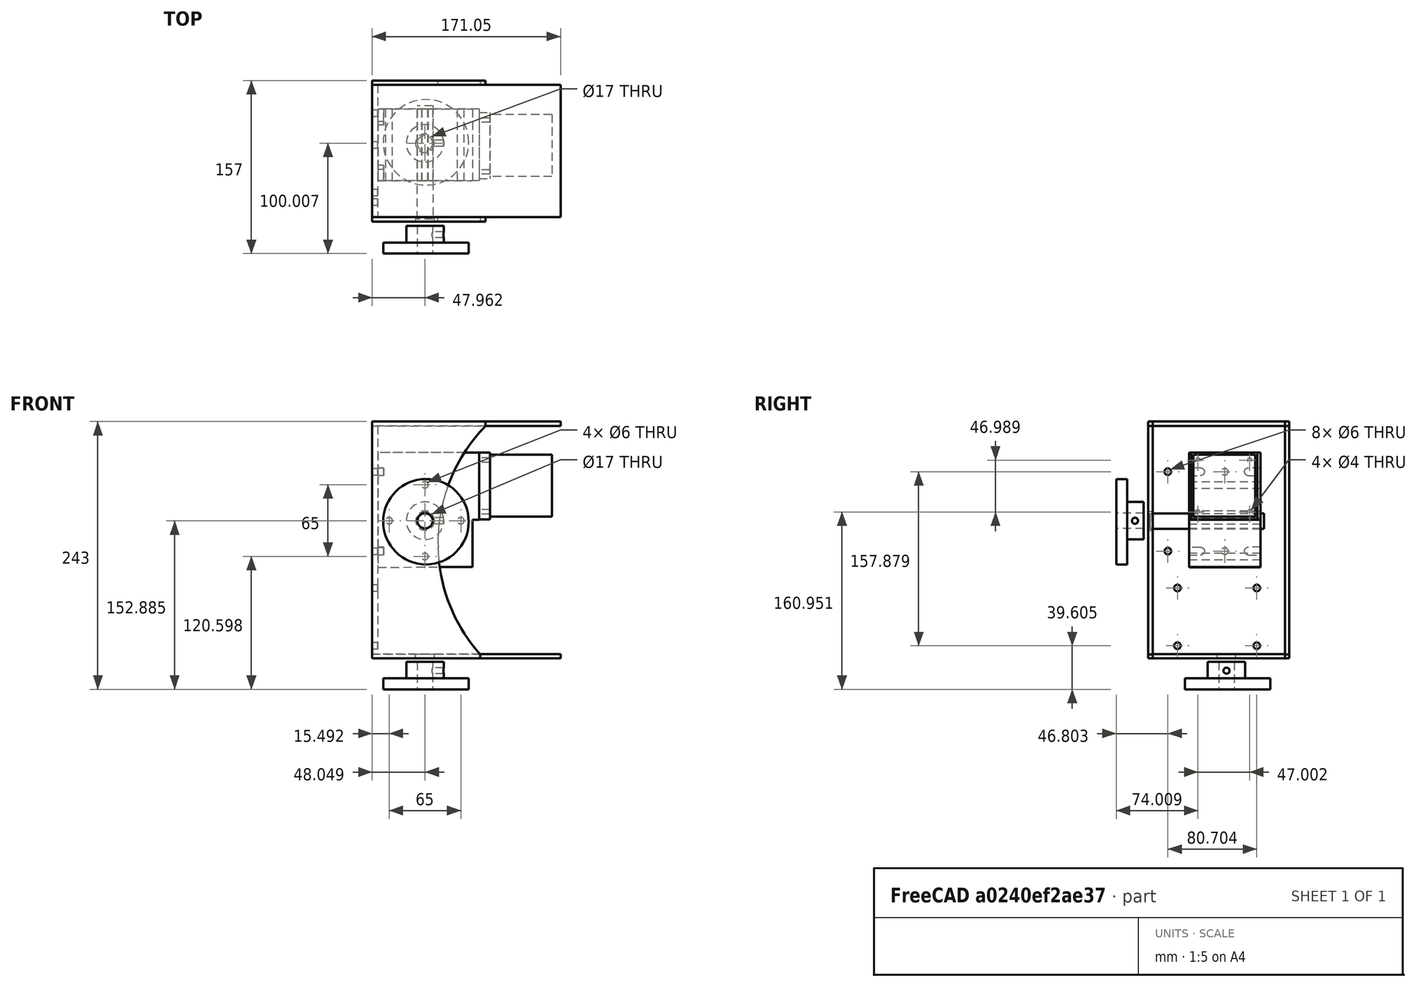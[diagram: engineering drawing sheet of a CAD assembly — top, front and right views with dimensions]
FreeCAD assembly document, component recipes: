
FREECAD ASSEMBLY — COMPONENT RECIPES ("az-el-rotor")

This assembly document has 15 components, labeled P0..P14 below (a component is one placed body or linked part). 15 of them carry a construction recipe — the FreeCAD feature program that regenerates the part from scratch, quoted from this document or its linked companion documents; the rest are supplied as boundary geometry only. No exploded tour is included for this assembly.
COMPONENT P0 — recipe-attached ("back-plate", modeled in this document).
Construction recipe (the document's own serialized feature program — sketch geometry with constraints, then the solid features built on it; lengths are millimeters unless a unit is written):

FEATURE [Sketcher::SketchObject] Sketch009
  MapMode = 5
  Placement = pos=(0,0,0) rot=(0.57735,0.57735,0.57735;2.0944rad)
  Support = -> [YZ_Plane004]
  sketch-geometry (24):
    g0: LineSegment [constr] StartX=-28 StartY=-262 StartZ=0 EndX=78 EndY=-262 EndZ=0
    g1: LineSegment [constr] StartX=78 StartY=-262 StartZ=0 EndX=78 EndY=-263 EndZ=0
    g2: LineSegment [constr] StartX=78 StartY=-263 StartZ=0 EndX=-28 EndY=-263 EndZ=0
    g3: LineSegment [constr] StartX=-28 StartY=-263 StartZ=0 EndX=-28 EndY=-262 EndZ=0
    g4: LineSegment [constr] StartX=78 StartY=-263 StartZ=0 EndX=88 EndY=-263 EndZ=0
    g5: LineSegment [constr] StartX=88 StartY=-263 StartZ=0 EndX=88 EndY=-80 EndZ=0
    g6: LineSegment [constr] StartX=88 StartY=-80 StartZ=0 EndX=78 EndY=-80 EndZ=0
    g7: LineSegment [constr] StartX=78 StartY=-80 StartZ=0 EndX=78 EndY=-263 EndZ=0
    g8: LineSegment [constr] StartX=88 StartY=-80 StartZ=0 EndX=78 EndY=-80 EndZ=0
    g9: LineSegment [constr] StartX=78 StartY=-80 StartZ=0 EndX=78 EndY=-60 EndZ=0
    g10: LineSegment [constr] StartX=78 StartY=-60 StartZ=0 EndX=88 EndY=-60 EndZ=0
    g11: LineSegment [constr] StartX=88 StartY=-60 StartZ=0 EndX=88 EndY=-80 EndZ=0
    g12: LineSegment [constr] StartX=88 StartY=-60 StartZ=0 EndX=-41 EndY=-60 EndZ=0
    g13: LineSegment [constr] StartX=-41 StartY=-60 StartZ=0 EndX=-41 EndY=-56 EndZ=0
    g14: LineSegment [constr] StartX=-41 StartY=-56 StartZ=0 EndX=88 EndY=-56 EndZ=0
    g15: LineSegment [constr] StartX=88 StartY=-56 StartZ=0 EndX=88 EndY=-60 EndZ=0
    g16: LineSegment [constr] StartX=-28 StartY=-263 StartZ=0 EndX=-32 EndY=-263 EndZ=0
    g17: LineSegment [constr] StartX=-32 StartY=-263 StartZ=0 EndX=-32 EndY=-53 EndZ=0
    g18: LineSegment [constr] StartX=-32 StartY=-53 StartZ=0 EndX=-28 EndY=-53 EndZ=0
    g19: LineSegment [constr] StartX=-28 StartY=-53 StartZ=0 EndX=-28 EndY=-263 EndZ=0
    g20: LineSegment StartX=88 StartY=-263 StartZ=0 EndX=-32 EndY=-263 EndZ=0
    g21: LineSegment StartX=-32 StartY=-263 StartZ=0 EndX=-32 EndY=-56 EndZ=0
    g22: LineSegment StartX=-32 StartY=-56 StartZ=0 EndX=88 EndY=-56 EndZ=0
    g23: LineSegment StartX=88 StartY=-56 StartZ=0 EndX=88 EndY=-263 EndZ=0
  constraints (53):
    c: Coincident(g0,g1)
    c: Coincident(g1,g2)
    c: Coincident(g2,g3)
    c: Coincident(g3,g0)
    c: Horizontal(g0)
    c: Horizontal(g2)
    c: Vertical(g1)
    c: Vertical(g3)
    c: Coincident(g4,g5)
    c: Coincident(g5,g6)
    c: Coincident(g6,g7)
    c: Coincident(g7,g4)
    c: Horizontal(g4)
    c: Horizontal(g6)
    c: Vertical(g5)
    c: Vertical(g7)
    c: Coincident(g4,g1)
    c: Coincident(g8,g9)
    c: Coincident(g9,g10)
    c: Coincident(g10,g11)
    c: Coincident(g11,g8)
    c: Horizontal(g8)
    c: Horizontal(g10)
    c: Vertical(g9)
    c: Vertical(g11)
    c: Coincident(g12,g13)
    c: Coincident(g13,g14)
    c: Coincident(g14,g15)
    c: Coincident(g15,g12)
    c: Horizontal(g12)
    c: Horizontal(g14)
    c: Vertical(g13)
    c: Vertical(g15)
    c: Coincident(g12,g10)
    c: Coincident(g16,g17)
    c: Coincident(g17,g18)
    c: Coincident(g18,g19)
    c: Coincident(g19,g16)
    c: Horizontal(g16)
    c: Horizontal(g18)
    c: Vertical(g17)
    c: Vertical(g19)
    c: Coincident(g16,g2)
    c: Coincident(g20,g21)
    c: Coincident(g21,g22)
    c: Coincident(g22,g23)
    c: Coincident(g23,g20)
    c: Horizontal(g20)
    c: Horizontal(g22)
    c: Vertical(g21)
    c: Vertical(g23)
    c: Coincident(g20,g4)
    c: PointOnObject(g21,g17)
FEATURE [PartDesign::Pad] Pad004
  AllowMultiFace = false
  Direction = (1,1,1)
  Length = 5
  Length2 = 100
  Placement = pos=(0,0,0) rot=(0.57735,0.57735,0.57735;2.0944rad)
  Profile = -> Sketch009
  Type = 0
FEATURE [Sketcher::SketchObject] Sketch010
  MapMode = 5
  Placement = pos=(4e-16,0,0) rot=(0.57735,0.57735,-0.57735;4.18879rad)
  Support = -> [Pad004]
  sketch-geometry (16):
    g0: Circle CenterX=33.537 CenterY=97.5713 CenterZ=0 NormalX=0 NormalY=0 NormalZ=1 AngleXU=0 Radius=3.67394
    g1: Circle CenterX=-18.1974 CenterY=97.5163 CenterZ=0 NormalX=0 NormalY=0 NormalZ=1 AngleXU=0 Radius=3.49495
    g2: LineSegment [constr] StartX=33.537 StartY=97.5713 StartZ=0 EndX=-18.1875 EndY=97.5713 EndZ=0
    g3: LineSegment [constr] StartX=-18.1875 StartY=97.5713 StartZ=0 EndX=-18.1875 EndY=169.553 EndZ=0
    g4: LineSegment [constr] StartX=-18.1875 StartY=169.553 StartZ=0 EndX=33.537 EndY=169.553 EndZ=0
    g5: LineSegment [constr] StartX=33.537 StartY=169.553 StartZ=0 EndX=33.537 EndY=97.5713 EndZ=0
    g6: Circle CenterX=-18.1875 CenterY=169.553 CenterZ=0 NormalX=0 NormalY=0 NormalZ=1 AngleXU=0 Radius=3.5641
    g7: Circle CenterX=33.537 CenterY=169.553 CenterZ=0 NormalX=0 NormalY=0 NormalZ=1 AngleXU=0 Radius=3.59605
    g8: LineSegment [constr] StartX=-9.48692 StartY=255.395 StartZ=0 EndX=62.5067 EndY=255.395 EndZ=0
    g9: LineSegment [constr] StartX=62.5067 StartY=255.395 StartZ=0 EndX=62.5067 EndY=203.001 EndZ=0
    g10: LineSegment [constr] StartX=62.5067 StartY=203.001 StartZ=0 EndX=-9.48692 EndY=203.001 EndZ=0
    g11: LineSegment [constr] StartX=-9.48692 StartY=203.001 StartZ=0 EndX=-9.48692 EndY=255.395 EndZ=0
    g12: Circle CenterX=-9.48692 CenterY=255.395 CenterZ=0 NormalX=0 NormalY=0 NormalZ=1 AngleXU=0 Radius=3.50608
    g13: Circle CenterX=62.5067 CenterY=255.395 CenterZ=0 NormalX=0 NormalY=0 NormalZ=1 AngleXU=0 Radius=3.47701
    g14: Circle CenterX=62.5067 CenterY=203.001 CenterZ=0 NormalX=0 NormalY=0 NormalZ=1 AngleXU=0 Radius=3.61631
    g15: Circle CenterX=-9.48692 CenterY=203.001 CenterZ=0 NormalX=0 NormalY=0 NormalZ=1 AngleXU=0 Radius=3.60277
  constraints (23):
    c: Coincident(g2,g3)
    c: Coincident(g3,g4)
    c: Coincident(g4,g5)
    c: Coincident(g5,g2)
    c: Horizontal(g2)
    c: Horizontal(g4)
    c: Vertical(g3)
    c: Vertical(g5)
    c: Coincident(g2,g0)
    c: Coincident(g6,g3)
    c: Coincident(g7,g4)
    c: Coincident(g8,g9)
    c: Coincident(g9,g10)
    c: Coincident(g10,g11)
    c: Coincident(g11,g8)
    c: Horizontal(g8)
    c: Horizontal(g10)
    c: Vertical(g9)
    c: Vertical(g11)
    c: Coincident(g12,g8)
    c: Coincident(g13,g8)
    c: Coincident(g14,g9)
    c: Coincident(g15,g10)
FEATURE [PartDesign::Hole] Hole002
  AllowMultiFace = false
  BaseFeature = -> Pad004
  Depth = 7
  DepthType = 0
  Diameter = 6
  DrillPoint = 1
  DrillPointAngle = 118
  HoleCutCountersinkAngle = 90
  HoleCutDepth = 0
  HoleCutDiameter = 0
  HoleCutType = 0
  ModelActualThread = false
  Placement = pos=(0,0,0) rot=(0.57735,0.57735,0.57735;2.0944rad)
  Profile = -> Sketch010
  Tapered = false
  TaperedAngle = 90
  ThreadAngle = 0
  ThreadClass = 0
  ThreadCutOffInner = 0
  ThreadCutOffOuter = 0
  ThreadDirection = 0
  ThreadFit = 0
  ThreadPitch = 0
  ThreadSize = 0
  ThreadType = 0
  Threaded = false
FEATURE [PartDesign::Body] Body004  label="back-plate"
  Group = -> [Sketch009,Pad004,Sketch010,Hole002]
  Origin = -> Origin004
  Placement = pos=(-94,0,0) rot=(0,0,1;0rad)
  Tip = -> Hole002
COMPONENT P1 — recipe-attached ("top-plate", modeled in this document).
Construction recipe (the document's own serialized feature program — sketch geometry with constraints, then the solid features built on it; lengths are millimeters unless a unit is written):

FEATURE [Sketcher::SketchObject] Sketch011
  MapMode = 5
  Support = -> [XY_Plane005]
  sketch-geometry (4):
    g0: LineSegment StartX=-94 StartY=88 StartZ=0 EndX=77.053 EndY=88 EndZ=0
    g1: LineSegment StartX=77.053 StartY=88 StartZ=0 EndX=77.053 EndY=-32 EndZ=0
    g2: LineSegment StartX=77.053 StartY=-32 StartZ=0 EndX=-94 EndY=-32 EndZ=0
    g3: LineSegment StartX=-94 StartY=-32 StartZ=0 EndX=-94 EndY=88 EndZ=0
  constraints (8):
    c: Coincident(g0,g1)
    c: Coincident(g1,g2)
    c: Coincident(g2,g3)
    c: Coincident(g3,g0)
    c: Horizontal(g0)
    c: Horizontal(g2)
    c: Vertical(g1)
    c: Vertical(g3)
FEATURE [PartDesign::Pad] Pad005
  AllowMultiFace = false
  Direction = (1,1,1)
  Length = 4
  Length2 = 100
  Profile = -> Sketch011
  Type = 0
FEATURE [PartDesign::Body] Body005  label="top-plate"
  Group = -> [Sketch011,Pad005]
  Origin = -> Origin005
  Placement = pos=(0,0,-56) rot=(0,0,1;0rad)
  Tip = -> Pad005
COMPONENT P2 — recipe-attached ("bottom-plate", modeled in this document).
Construction recipe (the document's own serialized feature program — sketch geometry with constraints, then the solid features built on it; lengths are millimeters unless a unit is written):

FEATURE [Sketcher::SketchObject] Sketch012
  MapMode = 5
  Support = -> [XY_Plane006]
  sketch-geometry (4):
    g0: LineSegment StartX=-93.9912 StartY=88.0053 StartZ=0 EndX=77 EndY=88.0053 EndZ=0
    g1: LineSegment StartX=77 StartY=88.0053 StartZ=0 EndX=77 EndY=-32 EndZ=0
    g2: LineSegment StartX=77 StartY=-32 StartZ=0 EndX=-93.9912 EndY=-32 EndZ=0
    g3: LineSegment StartX=-93.9912 StartY=-32 StartZ=0 EndX=-93.9912 EndY=88.0053 EndZ=0
  constraints (8):
    c: Coincident(g0,g1)
    c: Coincident(g1,g2)
    c: Coincident(g2,g3)
    c: Coincident(g3,g0)
    c: Horizontal(g0)
    c: Horizontal(g2)
    c: Vertical(g1)
    c: Vertical(g3)
FEATURE [PartDesign::Pad] Pad006
  AllowMultiFace = false
  Direction = (1,1,1)
  Length = 4
  Length2 = 100
  Profile = -> Sketch012
  Type = 0
FEATURE [Sketcher::SketchObject] Sketch013
  MapMode = 5
  Placement = pos=(0,0,0) rot=(1,0,0;3.14159rad)
  Support = -> [Pad006]
  sketch-geometry (1):
    g0: Circle CenterX=-46.0384 CenterY=-35.0069 CenterZ=0 NormalX=0 NormalY=0 NormalZ=1 AngleXU=0 Radius=10.0299
FEATURE [PartDesign::Hole] Hole003
  AllowMultiFace = false
  BaseFeature = -> Pad006
  Depth = 10
  DepthType = 0
  Diameter = 17
  DrillPoint = 1
  DrillPointAngle = 118
  HoleCutCountersinkAngle = 90
  HoleCutDepth = 0
  HoleCutDiameter = 0
  HoleCutType = 0
  ModelActualThread = false
  Profile = -> Sketch013
  Tapered = false
  TaperedAngle = 90
  ThreadAngle = 0
  ThreadClass = 0
  ThreadCutOffInner = 0
  ThreadCutOffOuter = 0
  ThreadDirection = 0
  ThreadFit = 0
  ThreadPitch = 0
  ThreadSize = 0
  ThreadType = 0
  Threaded = false
FEATURE [PartDesign::Body] Body006  label="bottom-plate"
  Group = -> [Sketch012,Pad006,Sketch013,Hole003]
  Origin = -> Origin006
  Placement = pos=(0,0,-267) rot=(0,0,1;0rad)
  Tip = -> Hole003
COMPONENT P3 — recipe-attached ("adapter", modeled in this document).
Construction recipe (the document's own serialized feature program — sketch geometry with constraints, then the solid features built on it; lengths are millimeters unless a unit is written):

FEATURE [Sketcher::SketchObject] Sketch014
  MapMode = 5
  Support = -> [XY_Plane007]
  sketch-geometry (1):
    g0: Circle CenterX=-46.1126 CenterY=35.0755 CenterZ=0 NormalX=0 NormalY=0 NormalZ=1 AngleXU=0 Radius=38.7738
FEATURE [PartDesign::Pad] Pad007
  AllowMultiFace = false
  Direction = (1,1,1)
  Length = 10
  Length2 = 100
  Profile = -> Sketch014
  Type = 0
FEATURE [Sketcher::SketchObject] Sketch015
  MapMode = 5
  Placement = pos=(0,0,0) rot=(1,0,0;3.14159rad)
  Support = -> [Pad007]
  sketch-geometry (4):
    g0: LineSegment [constr] StartX=-47 StartY=5 StartZ=0 EndX=-47 EndY=-81 EndZ=0
    g1: LineSegment [constr] StartX=-86 StartY=-36 StartZ=0 EndX=-6 EndY=-36 EndZ=0
    g2: Circle [constr] CenterX=-47 CenterY=-36 CenterZ=0 NormalX=0 NormalY=0 NormalZ=1 AngleXU=0 Radius=7
    g3: Circle CenterX=-47 CenterY=-36 CenterZ=0 NormalX=0 NormalY=0 NormalZ=1 AngleXU=0 Radius=17
  constraints (5):
    c: Vertical(g0)
    c: Horizontal(g1)
    c: PointOnObject(g2,g0)
    c: Diameter(g2) = 14
    c: Coincident(g3,g2)
FEATURE [PartDesign::Pad] Pad008
  AllowMultiFace = false
  BaseFeature = -> Pad007
  Direction = (1,1,1)
  Length = 15
  Length2 = 100
  Profile = -> Sketch015
  Type = 0
FEATURE [Sketcher::SketchObject] Sketch016
  MapMode = 5
  Placement = pos=(0,0,-15) rot=(1,0,0;3.14159rad)
  Support = -> [Pad008]
  sketch-geometry (3):
    g0: LineSegment [constr] StartX=-47.0041 StartY=-17.9869 StartZ=0 EndX=-47.0041 EndY=-57.2105 EndZ=0
    g1: LineSegment [constr] StartX=-67.0883 StartY=-35.9976 StartZ=0 EndX=-26.7183 EndY=-35.9976 EndZ=0
    g2: Circle CenterX=-47.0247 CenterY=-35.9976 CenterZ=0 NormalX=0 NormalY=0 NormalZ=1 AngleXU=0 Radius=7
  constraints (4):
    c: Vertical(g0)
    c: Horizontal(g1)
    c: PointOnObject(g2,g1)
    c: Diameter(g2) = 14
FEATURE [PartDesign::Hole] Hole004
  AllowMultiFace = false
  BaseFeature = -> Pad008
  Depth = 33
  DepthType = 0
  Diameter = 14
  DrillPoint = 1
  DrillPointAngle = 118
  HoleCutCountersinkAngle = 90
  HoleCutDepth = 0
  HoleCutDiameter = 0
  HoleCutType = 0
  ModelActualThread = false
  Profile = -> Sketch016
  Tapered = false
  TaperedAngle = 90
  ThreadAngle = 0
  ThreadClass = 0
  ThreadCutOffInner = 0
  ThreadCutOffOuter = 0
  ThreadDirection = 0
  ThreadFit = 0
  ThreadPitch = 0
  ThreadSize = 0
  ThreadType = 0
  Threaded = false
FEATURE [Sketcher::SketchObject] Sketch017
  MapMode = 5
  Placement = pos=(0,0,0) rot=(0.57735,0.57735,0.57735;2.0944rad)
  Support = -> [YZ_Plane007]
  sketch-geometry (1):
    g0: Circle CenterX=35.9745 CenterY=-6.96869 CenterZ=0 NormalX=0 NormalY=0 NormalZ=1 AngleXU=0 Radius=2.5
  constraints (1):
    c: Diameter(g0) = 5
FEATURE [PartDesign::Hole] Hole005
  AllowMultiFace = false
  BaseFeature = -> Hole004
  Depth = 43
  DepthType = 0
  Diameter = 5.5
  DrillPoint = 1
  DrillPointAngle = 118
  HoleCutCountersinkAngle = 90
  HoleCutDepth = 0
  HoleCutDiameter = 5
  HoleCutType = 0
  ModelActualThread = false
  Profile = -> Sketch017
  Tapered = false
  TaperedAngle = 90
  ThreadAngle = 60
  ThreadClass = 0
  ThreadCutOffInner = 0.0866025
  ThreadCutOffOuter = 0.173205
  ThreadDirection = 0
  ThreadFit = 0
  ThreadPitch = 0.8
  ThreadSize = 0
  ThreadType = 0
  Threaded = false
FEATURE [PartDesign::Body] Body007  label="adapter"
  Group = -> [Sketch014,Pad007,Sketch015,Pad008,Sketch016,Hole004,Sketch017,Hole005]
  Origin = -> Origin007
  Placement = pos=(1,71,-285) rot=(1,0,0;3.14159rad)
  Tip = -> Hole005
COMPONENT P4 — recipe-attached ("sideplate1", modeled in this document).
Construction recipe (the document's own serialized feature program — sketch geometry with constraints, then the solid features built on it; lengths are millimeters unless a unit is written):

FEATURE [Sketcher::SketchObject] Sketch018
  MapMode = 5
  Placement = pos=(0,0,0) rot=(1,0,0;1.5708rad)
  Support = -> [XZ_Plane008]
  sketch-geometry (7):
    g0: LineSegment StartX=-94 StartY=-52 StartZ=0 EndX=-94 EndY=-267 EndZ=0
    g1: LineSegment StartX=-94 StartY=-267 StartZ=0 EndX=3.97419 EndY=-267 EndZ=0
    g2: LineSegment StartX=9 StartY=-52 StartZ=0 EndX=-94 EndY=-52 EndZ=0
    g3: Circle [constr] CenterX=9 CenterY=-52 CenterZ=0 NormalX=0 NormalY=0 NormalZ=1 AngleXU=0 Radius=10
    g4: LineSegment StartX=9 StartY=-52 StartZ=0 EndX=9 EndY=-56 EndZ=0
    g5: LineSegment StartX=3.97419 StartY=-267 StartZ=0 EndX=3.97419 EndY=-263.283 EndZ=0
    g6: ArcOfCircle CenterX=117.845 CenterY=-162.341 CenterZ=0 NormalX=0 NormalY=0 NormalZ=1 AngleXU=0 Radius=152.17 StartAngle=2.36783 EndAngle=3.86687
  constraints (12):
    c: Vertical(g0)
    c: Coincident(g0,g1)
    c: Horizontal(g1)
    c: Coincident(g2,g0)
    c: Horizontal(g2)
    c: Coincident(g3,g2)
    c: Coincident(g4,g2)
    c: Vertical(g4)
    c: Vertical(g5)
    c: Coincident(g6,g4)
    c: Coincident(g6,g5)
    c: Coincident(g1,g5)
FEATURE [PartDesign::Pad] Pad009
  AllowMultiFace = false
  Direction = (1,1,1)
  Length = 4
  Length2 = 100
  Placement = pos=(0,0,0) rot=(1,0,0;1.5708rad)
  Profile = -> Sketch018
  Type = 0
FEATURE [Sketcher::SketchObject] Sketch020
  MapMode = 5
  Placement = pos=(0,-4,9e-16) rot=(1,0,0;1.5708rad)
  Support = -> [Pad009]
  sketch-geometry (1):
    g0: Circle CenterX=-45.9514 CenterY=-142.115 CenterZ=0 NormalX=0 NormalY=0 NormalZ=1 AngleXU=0 Radius=8.75
  constraints (1):
    c: Diameter(g0) = 17.5
FEATURE [PartDesign::Hole] Hole006
  AllowMultiFace = false
  BaseFeature = -> Pad009
  Depth = 25
  DepthType = 0
  Diameter = 17
  DrillPoint = 1
  DrillPointAngle = 118
  HoleCutCountersinkAngle = 90
  HoleCutDepth = 0
  HoleCutDiameter = 0
  HoleCutType = 0
  ModelActualThread = false
  Placement = pos=(0,0,0) rot=(1,0,0;1.5708rad)
  Profile = -> Sketch020
  Tapered = false
  TaperedAngle = 90
  ThreadAngle = 0
  ThreadClass = 0
  ThreadCutOffInner = 0
  ThreadCutOffOuter = 0
  ThreadDirection = 0
  ThreadFit = 0
  ThreadPitch = 0
  ThreadSize = 0
  ThreadType = 0
  Threaded = false
FEATURE [PartDesign::Body] Body008  label="sideplate1"
  Group = -> [Sketch018,Pad009,Sketch020,Hole006]
  Origin = -> Origin008
  Placement = pos=(0,-32,0) rot=(0,0,1;0rad)
  Tip = -> Hole006
COMPONENT P5 — recipe-attached ("sideplate002", modeled in this document).
Construction recipe (the document's own serialized feature program — sketch geometry with constraints, then the solid features built on it; lengths are millimeters unless a unit is written):

FEATURE [Sketcher::SketchObject] Sketch019
  MapMode = 5
  Placement = pos=(0,0,0) rot=(1,0,0;1.5708rad)
  Support = -> [XZ_Plane009]
  sketch-geometry (7):
    g0: LineSegment StartX=-94 StartY=-52 StartZ=0 EndX=-94 EndY=-267 EndZ=0
    g1: LineSegment StartX=-94 StartY=-267 StartZ=0 EndX=3.97419 EndY=-267 EndZ=0
    g2: LineSegment StartX=9 StartY=-52 StartZ=0 EndX=-94 EndY=-52 EndZ=0
    g3: Circle [constr] CenterX=9 CenterY=-52 CenterZ=0 NormalX=0 NormalY=0 NormalZ=1 AngleXU=0 Radius=10
    g4: LineSegment StartX=9 StartY=-52 StartZ=0 EndX=9 EndY=-56 EndZ=0
    g5: LineSegment StartX=3.97419 StartY=-267 StartZ=0 EndX=3.97419 EndY=-263.283 EndZ=0
    g6: ArcOfCircle CenterX=117.845 CenterY=-162.341 CenterZ=0 NormalX=0 NormalY=0 NormalZ=1 AngleXU=0 Radius=152.17 StartAngle=2.36783 EndAngle=3.86687
  constraints (12):
    c: Vertical(g0)
    c: Coincident(g0,g1)
    c: Horizontal(g1)
    c: Coincident(g2,g0)
    c: Horizontal(g2)
    c: Coincident(g3,g2)
    c: Coincident(g4,g2)
    c: Vertical(g4)
    c: Vertical(g5)
    c: Coincident(g6,g4)
    c: Coincident(g6,g5)
    c: Coincident(g1,g5)
FEATURE [PartDesign::Pad] Pad010
  AllowMultiFace = false
  Direction = (1,1,1)
  Length = 4
  Length2 = 100
  Placement = pos=(0,0,0) rot=(1,0,0;1.5708rad)
  Profile = -> Sketch019
  Type = 0
FEATURE [PartDesign::Body] Body009  label="sideplate002"
  Group = -> [Sketch019,Pad010]
  Origin = -> Origin009
  Placement = pos=(0,92,0) rot=(0,0,1;0rad)
  Tip = -> Pad010
COMPONENT P6 — recipe-attached ("adapter001", modeled in this document).
Construction recipe (the document's own serialized feature program — sketch geometry with constraints, then the solid features built on it; lengths are millimeters unless a unit is written):

FEATURE [Sketcher::SketchObject] Sketch021
  MapMode = 5
  Support = -> [XY_Plane010]
  sketch-geometry (1):
    g0: Circle CenterX=-46.1126 CenterY=35.0755 CenterZ=0 NormalX=0 NormalY=0 NormalZ=1 AngleXU=0 Radius=38.7738
FEATURE [PartDesign::Pad] Pad011
  AllowMultiFace = false
  Direction = (1,1,1)
  Length = 10
  Length2 = 100
  Profile = -> Sketch021
  Type = 0
FEATURE [Sketcher::SketchObject] Sketch022
  MapMode = 5
  Placement = pos=(0,0,0) rot=(0.57735,0.57735,0.57735;2.0944rad)
  Support = -> [YZ_Plane010]
  sketch-geometry (1):
    g0: Circle CenterX=35.9745 CenterY=-6.96869 CenterZ=0 NormalX=0 NormalY=0 NormalZ=1 AngleXU=0 Radius=2.5
  constraints (1):
    c: Diameter(g0) = 5
FEATURE [Sketcher::SketchObject] Sketch024
  MapMode = 5
  Placement = pos=(0,0,0) rot=(1,0,0;3.14159rad)
  Support = -> [Pad011]
  sketch-geometry (4):
    g0: LineSegment [constr] StartX=-47 StartY=5 StartZ=0 EndX=-47 EndY=-81 EndZ=0
    g1: LineSegment [constr] StartX=-86 StartY=-36 StartZ=0 EndX=-6 EndY=-36 EndZ=0
    g2: Circle [constr] CenterX=-47 CenterY=-36 CenterZ=0 NormalX=0 NormalY=0 NormalZ=1 AngleXU=0 Radius=7
    g3: Circle CenterX=-47 CenterY=-36 CenterZ=0 NormalX=0 NormalY=0 NormalZ=1 AngleXU=0 Radius=17
  constraints (5):
    c: Vertical(g0)
    c: Horizontal(g1)
    c: PointOnObject(g2,g0)
    c: Diameter(g2) = 14
    c: Coincident(g3,g2)
FEATURE [PartDesign::Pad] Pad012
  AllowMultiFace = false
  BaseFeature = -> Pad011
  Direction = (1,1,1)
  Length = 15
  Length2 = 100
  Profile = -> Sketch024
  Type = 0
FEATURE [Sketcher::SketchObject] Sketch023
  MapMode = 5
  Placement = pos=(0,0,-15) rot=(1,0,0;3.14159rad)
  Support = -> [Pad012]
  sketch-geometry (3):
    g0: LineSegment [constr] StartX=-47.0041 StartY=-17.9869 StartZ=0 EndX=-47.0041 EndY=-57.2105 EndZ=0
    g1: LineSegment [constr] StartX=-67.0883 StartY=-35.9976 StartZ=0 EndX=-26.7183 EndY=-35.9976 EndZ=0
    g2: Circle CenterX=-47.0247 CenterY=-35.9976 CenterZ=0 NormalX=0 NormalY=0 NormalZ=1 AngleXU=0 Radius=7
  constraints (4):
    c: Vertical(g0)
    c: Horizontal(g1)
    c: PointOnObject(g2,g1)
    c: Diameter(g2) = 14
FEATURE [PartDesign::Hole] Hole007
  AllowMultiFace = false
  BaseFeature = -> Pad012
  Depth = 33
  DepthType = 0
  Diameter = 14
  DrillPoint = 1
  DrillPointAngle = 118
  HoleCutCountersinkAngle = 90
  HoleCutDepth = 0
  HoleCutDiameter = 0
  HoleCutType = 0
  ModelActualThread = false
  Profile = -> Sketch023
  Tapered = false
  TaperedAngle = 90
  ThreadAngle = 0
  ThreadClass = 0
  ThreadCutOffInner = 0
  ThreadCutOffOuter = 0
  ThreadDirection = 0
  ThreadFit = 0
  ThreadPitch = 0
  ThreadSize = 0
  ThreadType = 0
  Threaded = false
FEATURE [PartDesign::Hole] Hole008
  AllowMultiFace = false
  BaseFeature = -> Hole007
  Depth = 43
  DepthType = 0
  Diameter = 5.5
  DrillPoint = 1
  DrillPointAngle = 118
  HoleCutCountersinkAngle = 90
  HoleCutDepth = 0
  HoleCutDiameter = 5
  HoleCutType = 0
  ModelActualThread = false
  Profile = -> Sketch022
  Tapered = false
  TaperedAngle = 90
  ThreadAngle = 60
  ThreadClass = 0
  ThreadCutOffInner = 0.0866025
  ThreadCutOffOuter = 0.173205
  ThreadDirection = 0
  ThreadFit = 0
  ThreadPitch = 0.8
  ThreadSize = 0
  ThreadType = 0
  Threaded = false
FEATURE [PartDesign::Body] Body010  label="adapter001"
  Group = -> [Sketch021,Pad011,Sketch024,Pad012,Sketch023,Hole007,Sketch022,Hole008]
  Origin = -> Origin010
  Placement = pos=(1,-55,-178) rot=(1,0,0;1.5708rad)
  Tip = -> Hole008
COMPONENT P7 — recipe-attached ("motor001", modeled in this document).
Construction recipe (the document's own serialized feature program — sketch geometry with constraints, then the solid features built on it; lengths are millimeters unless a unit is written):

FEATURE [Sketcher::SketchObject] Sketch001
  MapMode = 5
  Placement = pos=(0,0,0) rot=(1,0,0;1.5708rad)
  Support = -> [XZ_Plane001]
  sketch-geometry (4):
    g0: LineSegment StartX=-11.8481 StartY=194.05 StartZ=0 EndX=-68.2481 EndY=194.05 EndZ=0
    g1: LineSegment StartX=-68.2481 StartY=194.05 StartZ=0 EndX=-68.2481 EndY=137.65 EndZ=0
    g2: LineSegment StartX=-68.2481 StartY=137.65 StartZ=0 EndX=-11.8481 EndY=137.65 EndZ=0
    g3: LineSegment StartX=-11.8481 StartY=137.65 StartZ=0 EndX=-11.8481 EndY=194.05 EndZ=0
  constraints (10):
    c: Coincident(g0,g1)
    c: Coincident(g1,g2)
    c: Coincident(g2,g3)
    c: Coincident(g3,g0)
    c: Horizontal(g0)
    c: Horizontal(g2)
    c: Vertical(g1)
    c: Vertical(g3)
    c: DistanceX(g0,g0) = 56.4
    c: DistanceY(g3,g3) = 56.4
FEATURE [PartDesign::Pad] Pad
  AllowMultiFace = false
  Direction = (1,1,1)
  Length = 56
  Length2 = 100
  Placement = pos=(0,0,0) rot=(1,0,0;1.5708rad)
  Profile = -> Sketch001
  Type = 0
FEATURE [PartDesign::Body] Body001  label="motor"
  Group = -> [Sketch001,Pad]
  Origin = -> Origin001
  Placement = pos=(81,61,-276) rot=(0,0,1;0rad)
  Tip = -> Pad
COMPONENT P8 — recipe-attached ("motor-mount001", modeled in this document).
Construction recipe (the document's own serialized feature program — sketch geometry with constraints, then the solid features built on it; lengths are millimeters unless a unit is written):

FEATURE [Sketcher::SketchObject] Sketch
  MapMode = 5
  Placement = pos=(0,0,0) rot=(1,0,0;1.5708rad)
  Support = -> [XZ_Plane]
  sketch-geometry (4):
    g0: LineSegment StartX=103.932 StartY=89.9717 StartZ=0 EndX=43.9326 EndY=89.9717 EndZ=0
    g1: LineSegment StartX=43.9326 StartY=89.9717 StartZ=0 EndX=43.9326 EndY=29.0926 EndZ=0
    g2: LineSegment StartX=43.9326 StartY=29.0926 StartZ=0 EndX=103.932 EndY=29.0926 EndZ=0
    g3: LineSegment StartX=103.932 StartY=29.0926 StartZ=0 EndX=103.932 EndY=89.9717 EndZ=0
  constraints (8):
    c: Coincident(g0,g1)
    c: Coincident(g1,g2)
    c: Coincident(g2,g3)
    c: Coincident(g3,g0)
    c: Horizontal(g0)
    c: Horizontal(g2)
    c: Vertical(g1)
    c: Vertical(g3)
FEATURE [PartDesign::Pad] Pad001
  AllowMultiFace = false
  Direction = (1,1,1)
  Length = 10
  Length2 = 100
  Placement = pos=(0,0,0) rot=(1,0,0;1.5708rad)
  Profile = -> Sketch
  Type = 0
FEATURE [Sketcher::SketchObject] Sketch002
  MapMode = 5
  Placement = pos=(0,-10,2.2e-15) rot=(1,0,0;1.5708rad)
  Support = -> [Pad001]
  sketch-geometry (8):
    g0: LineSegment [constr] StartX=97.011 StartY=82.9397 StartZ=0 EndX=50.0093 EndY=82.9397 EndZ=0
    g1: LineSegment [constr] StartX=50.0093 StartY=82.9397 StartZ=0 EndX=50.0093 EndY=35.9508 EndZ=0
    g2: LineSegment [constr] StartX=50.0093 StartY=35.9508 StartZ=0 EndX=97.011 EndY=35.9508 EndZ=0
    g3: LineSegment [constr] StartX=97.011 StartY=35.9508 StartZ=0 EndX=97.011 EndY=82.9397 EndZ=0
    g4: Circle CenterX=97.011 CenterY=82.9397 CenterZ=0 NormalX=0 NormalY=0 NormalZ=1 AngleXU=0 Radius=2.60112
    g5: Circle CenterX=50.0093 CenterY=82.9397 CenterZ=0 NormalX=0 NormalY=0 NormalZ=1 AngleXU=0 Radius=2.14953
    g6: Circle CenterX=50.0093 CenterY=35.9508 CenterZ=0 NormalX=0 NormalY=0 NormalZ=1 AngleXU=0 Radius=2.21763
    g7: Circle CenterX=97.011 CenterY=35.9508 CenterZ=0 NormalX=0 NormalY=0 NormalZ=1 AngleXU=0 Radius=2.02514
  constraints (12):
    c: Coincident(g0,g1)
    c: Coincident(g1,g2)
    c: Coincident(g2,g3)
    c: Coincident(g3,g0)
    c: Horizontal(g0)
    c: Horizontal(g2)
    c: Vertical(g1)
    c: Vertical(g3)
    c: Coincident(g4,g0)
    c: Coincident(g5,g0)
    c: Coincident(g6,g1)
    c: Coincident(g7,g2)
FEATURE [PartDesign::Hole] Hole
  AllowMultiFace = false
  BaseFeature = -> Pad001
  Depth = 25
  DepthType = 0
  Diameter = 4
  DrillPoint = 1
  DrillPointAngle = 118
  HoleCutCountersinkAngle = 90
  HoleCutDepth = 0
  HoleCutDiameter = 0
  HoleCutType = 0
  ModelActualThread = false
  Placement = pos=(0,0,0) rot=(1,0,0;1.5708rad)
  Profile = -> Sketch002
  Tapered = false
  TaperedAngle = 90
  ThreadAngle = 0
  ThreadClass = 0
  ThreadCutOffInner = 0
  ThreadCutOffOuter = 0
  ThreadDirection = 0
  ThreadFit = 0
  ThreadPitch = 0
  ThreadSize = 0
  ThreadType = 0
  Threaded = false
FEATURE [PartDesign::Body] Body  label="motor-mount"
  Group = -> [Sketch,Pad001,Sketch002,Hole]
  Origin = -> Origin
  Placement = pos=(3,-41,-170) rot=(0,0,1;1.5708rad)
  Tip = -> Hole
COMPONENT P9 — recipe-attached ("gearbox001", modeled in this document).
Construction recipe (the document's own serialized feature program — sketch geometry with constraints, then the solid features built on it; lengths are millimeters unless a unit is written):

FEATURE [Sketcher::SketchObject] Sketch003
  MapMode = 5
  Placement = pos=(0,0,0) rot=(1,0,0;1.5708rad)
  Support = -> [XZ_Plane002]
  sketch-geometry (9):
    g0: LineSegment [constr] StartX=-113.706 StartY=-142.169 StartZ=0 EndX=6.22488 EndY=-142.169 EndZ=0
    g1: LineSegment [constr] StartX=-45.8819 StartY=-179.611 StartZ=0 EndX=-45.8819 EndY=-105.711 EndZ=0
    g2: Circle [constr] CenterX=-45.9137 CenterY=-142.169 CenterZ=0 NormalX=0 NormalY=0 NormalZ=1 AngleXU=0 Radius=32.5
    g3: LineSegment StartX=3 StartY=-80 StartZ=0 EndX=-88.6238 EndY=-80 EndZ=0
    g4: LineSegment StartX=-88.6238 StartY=-80 StartZ=0 EndX=-88.5635 EndY=-184.211 EndZ=0
    g5: LineSegment StartX=-88.5635 StartY=-184.211 StartZ=0 EndX=-3 EndY=-184 EndZ=0
    g6: LineSegment StartX=-3 StartY=-184 StartZ=0 EndX=-3 EndY=-141 EndZ=0
    g7: LineSegment StartX=3 StartY=-141 StartZ=0 EndX=-3 EndY=-141 EndZ=0
    g8: LineSegment StartX=3 StartY=-141 StartZ=0 EndX=3 EndY=-80 EndZ=0
  constraints (6):
    c: Horizontal(g0)
    c: Vertical(g1)
    c: PointOnObject(g2,g0)
    c: Diameter(g2) = 65
    c: Coincident(g3,g4)
    c: Coincident(g4,g5)
FEATURE [PartDesign::Pad] Pad002
  AllowMultiFace = false
  Direction = (1,1,1)
  Length = 65
  Length2 = 100
  Placement = pos=(0,0,0) rot=(1,0,0;1.5708rad)
  Profile = -> Sketch003
  Type = 0
FEATURE [Sketcher::SketchObject] Sketch004
  MapMode = 5
  Placement = pos=(0,-65,1.43e-14) rot=(1,0,0;1.5708rad)
  Support = -> [Pad002]
  sketch-geometry (6):
    g0: Circle [constr] CenterX=-46.0078 CenterY=-141.902 CenterZ=0 NormalX=0 NormalY=0 NormalZ=1 AngleXU=0 Radius=32.5
    g1: LineSegment [constr] StartX=-46.0078 StartY=-141.902 StartZ=0 EndX=-46.0078 EndY=-102 EndZ=0
    g2: Circle CenterX=-46 CenterY=-109.402 CenterZ=0 NormalX=0 NormalY=0 NormalZ=1 AngleXU=0 Radius=3.60206
    g3: Circle CenterX=-13.5079 CenterY=-142 CenterZ=0 NormalX=0 NormalY=0 NormalZ=1 AngleXU=0 Radius=2.2381
    g4: Circle CenterX=-46 CenterY=-174.402 CenterZ=0 NormalX=0 NormalY=0 NormalZ=1 AngleXU=0 Radius=2.56856
    g5: Circle CenterX=-78.5076 CenterY=-142 CenterZ=0 NormalX=0 NormalY=0 NormalZ=1 AngleXU=0 Radius=1.48182
  constraints (7):
    c: Diameter(g0) = 65
    c: Coincident(g1,g0)
    c: Vertical(g1)
    c: PointOnObject(g2,g0)
    c: PointOnObject(g3,g0)
    c: PointOnObject(g4,g0)
    c: PointOnObject(g5,g0)
FEATURE [PartDesign::Hole] Hole001
  AllowMultiFace = false
  BaseFeature = -> Pad002
  Depth = 72
  DepthType = 0
  Diameter = 6
  DrillPoint = 1
  DrillPointAngle = 118
  HoleCutCountersinkAngle = 90
  HoleCutDepth = 0
  HoleCutDiameter = 0
  HoleCutType = 0
  ModelActualThread = false
  Placement = pos=(0,0,0) rot=(1,0,0;1.5708rad)
  Profile = -> Sketch004
  Tapered = false
  TaperedAngle = 90
  ThreadAngle = 0
  ThreadClass = 0
  ThreadCutOffInner = 0
  ThreadCutOffOuter = 0
  ThreadDirection = 0
  ThreadFit = 0
  ThreadPitch = 0
  ThreadSize = 0
  ThreadType = 0
  Threaded = false
FEATURE [Sketcher::SketchObject] Sketch005
  MapMode = 5
  Placement = pos=(0,-65,1.43e-14) rot=(1,0,0;1.5708rad)
  Support = -> [Hole001]
  sketch-geometry (5):
    g0: ArcOfCircle CenterX=-45.9597 CenterY=-141.985 CenterZ=0 NormalX=0 NormalY=0 NormalZ=1 AngleXU=0 Radius=7 StartAngle=1.94945 EndAngle=7.48847
    g1: LineSegment [constr] StartX=-48.5474 StartY=-132.991 StartZ=0 EndX=-43.4577 EndY=-132.991 EndZ=0
    g2: LineSegment StartX=-48.5474 StartY=-135.481 StartZ=0 EndX=-48.5474 EndY=-132.991 EndZ=0
    g3: LineSegment StartX=-48.5474 StartY=-132.991 StartZ=0 EndX=-43.4577 EndY=-132.991 EndZ=0
    g4: LineSegment StartX=-43.4577 StartY=-132.991 StartZ=0 EndX=-43.4577 EndY=-135.447 EndZ=0
  constraints (8):
    c: Horizontal(g1)
    c: Coincident(g2,g1)
    c: Vertical(g2)
    c: Coincident(g3,g1)
    c: Vertical(g4)
    c: Coincident(g2,g3)
    c: Coincident(g0,g4)
    c: Coincident(g3,g4)
FEATURE [PartDesign::Pocket] Pocket
  AllowMultiFace = false
  BaseFeature = -> Hole001
  Length = 72
  Length2 = 100
  Placement = pos=(0,0,0) rot=(1,0,0;1.5708rad)
  Profile = -> Sketch005
  Type = 0
FEATURE [Sketcher::SketchObject] Sketch007
  MapMode = 5
  Placement = pos=(-88.6701,0,-0.0513552) rot=(0.707312,0,-0.706902;3.14159rad)
  Support = -> [Pocket]
  sketch-geometry (4):
    g0: LineSegment StartX=94 StartY=65.9617 StartZ=0 EndX=101.06 EndY=65.9617 EndZ=0
    g1: LineSegment StartX=101.06 StartY=65.9617 StartZ=0 EndX=101.06 EndY=54.6023 EndZ=0
    g2: LineSegment StartX=94 StartY=54.5531 StartZ=0 EndX=94 EndY=65.9617 EndZ=0
    g3: ArcOfCircle CenterX=97.5304 CenterY=54.5531 CenterZ=0 NormalX=0 NormalY=0 NormalZ=1 AngleXU=0 Radius=3.53039 StartAngle=3.14159 EndAngle=6.29711
  constraints (7):
    c: Coincident(g0,g1)
    c: Coincident(g2,g0)
    c: Horizontal(g0)
    c: Vertical(g1)
    c: Vertical(g2)
    c: Coincident(g3,g1)
    c: Coincident(g2,g3)
FEATURE [PartDesign::Pocket] Pocket001
  AllowMultiFace = false
  BaseFeature = -> Pocket
  Length = 5
  Length2 = 100
  Placement = pos=(0,0,0) rot=(1,0,0;1.5708rad)
  Profile = -> Sketch007
  Type = 0
FEATURE [PartDesign::LinearPattern] LinearPattern
  BaseFeature = -> Pocket001
  Direction = -> Sketch007 [H_Axis]
  Length = 72
  Occurrences = 2
  Originals = -> [Pocket001]
  Placement = pos=(0,0,0) rot=(1,0,0;1.5708rad)
FEATURE [Sketcher::SketchObject] Sketch008
  MapMode = 5
  Placement = pos=(-88.6701,0,-0.0513552) rot=(0.707312,0,-0.706902;3.14159rad)
  Support = -> [LinearPattern]
  sketch-geometry (5):
    g0: LineSegment [constr] StartX=97.5242 StartY=54.9703 StartZ=0 EndX=97.5242 EndY=-5.59938 EndZ=0
    g1: ArcOfCircle CenterX=97.5242 CenterY=11.0213 CenterZ=0 NormalX=0 NormalY=0 NormalZ=1 AngleXU=0 Radius=3.60435 StartAngle=6.27818 EndAngle=9.4465
    g2: LineSegment StartX=101.128 StartY=11.0032 StartZ=0 EndX=101.128 EndY=-1.64086 EndZ=0
    g3: LineSegment StartX=101.128 StartY=-1.64086 StartZ=0 EndX=93.9207 EndY=-1.64086 EndZ=0
    g4: LineSegment StartX=93.9207 StartY=-1.64086 StartZ=0 EndX=93.9207 EndY=10.943 EndZ=0
  constraints (9):
    c: Vertical(g0)
    c: PointOnObject(g1,g0)
    c: Coincident(g2,g3)
    c: Coincident(g3,g4)
    c: Horizontal(g3)
    c: Vertical(g2)
    c: Vertical(g4)
    c: Coincident(g1,g4)
    c: Coincident(g2,g1)
FEATURE [PartDesign::Pocket] Pocket002
  AllowMultiFace = false
  BaseFeature = -> LinearPattern
  Length = 5
  Length2 = 100
  Placement = pos=(0,0,0) rot=(1,0,0;1.5708rad)
  Profile = -> Sketch008
  Type = 0
FEATURE [PartDesign::LinearPattern] LinearPattern001
  BaseFeature = -> Pocket002
  Direction = -> Sketch008 [H_Axis]
  Length = 72
  Occurrences = 2
  Originals = -> [Pocket002]
  Placement = pos=(0,0,0) rot=(1,0,0;1.5708rad)
FEATURE [PartDesign::Body] Body002  label="gearbox"
  Group = -> [Sketch003,Pad002,Sketch004,Hole001,Sketch005,Pocket,Sketch007,Pocket001,LinearPattern,Sketch008,Pocket002,LinearPattern001]
  Origin = -> Origin002
  Placement = pos=(0,66,0) rot=(0,0,1;0rad)
  Tip = -> LinearPattern001
COMPONENT P10 — recipe-attached ("Body004", modeled in this document).
Construction recipe (the document's own serialized feature program — sketch geometry with constraints, then the solid features built on it; lengths are millimeters unless a unit is written):

FEATURE [Sketcher::SketchObject] Sketch006
  MapMode = 5
  Placement = pos=(0,0,0) rot=(1,0,0;1.5708rad)
  Support = -> [XZ_Plane003]
  sketch-geometry (1):
    g0: Circle CenterX=-37.9108 CenterY=-368.292 CenterZ=0 NormalX=0 NormalY=0 NormalZ=1 AngleXU=0 Radius=7
  constraints (1):
    c: Diameter(g0) = 14
FEATURE [PartDesign::Pad] Pad003
  AllowMultiFace = false
  Direction = (1,1,1)
  Length = 103
  Length2 = 100
  Placement = pos=(0,0,0) rot=(1,0,0;1.5708rad)
  Profile = -> Sketch006
  Type = 0
FEATURE [PartDesign::Body] Body003
  Group = -> [Sketch006,Pad003]
  Origin = -> Origin003
  Placement = pos=(-8,69,226) rot=(0,0,1;0rad)
  Tip = -> Pad003
COMPONENT P11 — same part as P7; its construction recipe is shown at P7.
COMPONENT P12 — same part as P8; its construction recipe is shown at P8.
COMPONENT P13 — same part as P9; its construction recipe is shown at P9.
COMPONENT P14 — same part as P10; its construction recipe is shown at P10.
PROVENANCE & LICENSES
A FreeCAD (.FCStd) document from a public repository crawl; recipes are the document's own serialized feature recipes (and, for linked parts, companion documents' recipes).
License: as declared in the source repository (recorded in the dataset sidecar).
